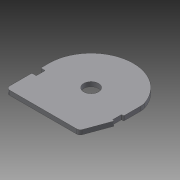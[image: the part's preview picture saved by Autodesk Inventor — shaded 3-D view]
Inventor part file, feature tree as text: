
AUTODESK INVENTOR PART (.ipt)
format: ipt  version: 2015 (Build 190159000, 159)  size: 119,296 bytes
history: native  units: mm
features: fillet x3, extrude x1, sketch x1
ambient origin geometry x8: Origin, YZ Plane, XZ Plane, XY Plane, X Axis, Y Axis, Z Axis, Center Point
bodies: Solid1 (feature_tree)
feature tree (5):
  extrude  "Extrusion1"  Depth=57.0mm
  fillet  "Fillet1"  Radius=20.0mm
  fillet  "Fillet2"  Radius=99.0mm
  fillet  "Fillet3"  Radius=6.0mm
  sketch  "Sketch1"  dims[d0=20.0mm d1=57.0mm d2=20.0mm d3=99.0mm d4=6.0mm d5=19.198622mm d6=3.0mm d7=12.0mm d8=58.0mm d9=12.0mm d10=55.0mm d11=47.0mm d12=6.0mm d13=0.0mm d14=0.5mm d15=1.0mm d16=5.0mm]
